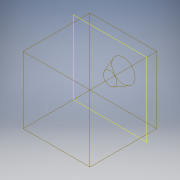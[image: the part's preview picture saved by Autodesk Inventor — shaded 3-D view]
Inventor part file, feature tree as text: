
AUTODESK INVENTOR PART (.ipt)
format: ipt  version: 2019.1 (Build 231200000, 200)  size: 126,976 bytes
history: native  units: mm
features: sketch x3, other x2, extrude x1, loft x1
ambient origin geometry x8: Origin, YZ Plane, XZ Plane, XY Plane, X Axis, Y Axis, Z Axis, Center Point
bodies: Body1 (feature_tree)
feature tree (7):
  other  "ソリッド1"
  extrude  "押し出し1"  Depth=2000.0mm
  sketch  "スケッチ2"
  other  "作業平面1"
  loft  "ロフト1"
  sketch  "スケッチ1"
  sketch  "スケッチ3"
